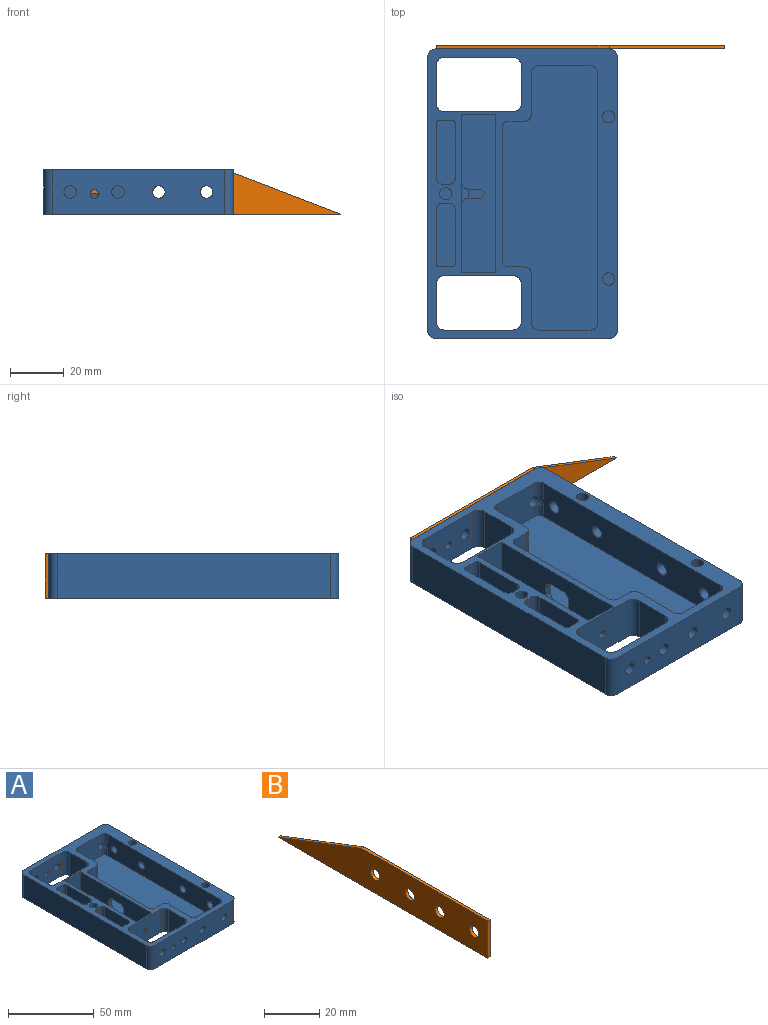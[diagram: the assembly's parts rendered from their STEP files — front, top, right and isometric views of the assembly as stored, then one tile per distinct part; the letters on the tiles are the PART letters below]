
ASSEMBLY  parts=2 mates=1
PART A: 110 faces, bbox 70.7x108x16.5 mm
  f0: plane 107.95x70.68mm, normal (0,0,1), area 2195.9mm2, adj f1,f2,f3,f7,f8,f9,f11,f12
  f1: plane 101.6x16.51mm, normal (1,0,0), area 1608mm2, adj f0,f14,f31,f32,f97,f98,f99,f100
  f2: plane 95.95x15.24mm, normal (-1,0,0), area 1357mm2, adj f0,f34,f85,f86,f87,f88,f89,f90
  f3: plane 49.23x15.24mm, normal (1,0,0), area 648.4mm2, adj f0,f34,f70,f71,f72,f73,f74,f75
  f4: plane 6.35x4.9mm, normal (0,1,0), area 31.1mm2, adj f6,f34,f102,f105
  f5: plane 6.35x4.9mm, normal (0,-1,0), area 31.1mm2, adj f6,f34,f101,f103
  f6: plane 6.52x3.24mm, normal (0,0,1), area 18.5mm2, adj f4,f5,f101,f102,f104
  f7: plane 64.33x16.51mm, normal (0,1,0), area 984.4mm2, adj f0,f11,f31,f32,f59,f66,f67,f68
  f8: plane 64.33x16.51mm, normal (0,-1,0), area 984.4mm2, adj f0,f13,f14,f32,f58,f62,f63,f64
  f9: plane 58.93x15.24mm, normal (1,0,0), area 824.1mm2, adj f0,f34,f60,f61,f103,f104,f105
  f10: cylinder r=1.63mm len=3.27mm, axis (0,-1,0), area 10.4mm2, adj f15,f60
  f11: cylinder r=3.17mm len=16.51mm, axis (0,0,-1), area 82.3mm2, adj f0,f7,f12,f32
  f12: plane 101.6x16.51mm, normal (-1,0,0), area 1677.4mm2, adj f0,f11,f13,f32
  f13: cylinder r=3.17mm len=16.51mm, axis (0,0,-1), area 82.3mm2, adj f0,f8,f12,f32
  f14: cylinder r=3.17mm len=16.51mm, axis (0,0,-1), area 82.3mm2, adj f0,f1,f8,f32
  f15: plane 25.4x16.51mm, normal (0,1,0), area 411mm2, adj f0,f10,f16,f29,f32
  f16: cylinder r=3.17mm len=16.51mm, axis (0,0,-1), area 82.3mm2, adj f0,f15,f17,f32
  f17: plane 16.51x13.97mm, normal (1,0,0), area 230.6mm2, adj f0,f16,f18,f32
  f18: cylinder r=3.17mm len=16.51mm, axis (0,0,-1), area 82.3mm2, adj f0,f17,f19,f32
  f19: plane 25.4x16.51mm, normal (0,-1,0), area 376.3mm2, adj f0,f18,f20,f32,f59,f68,f69
  f20: cylinder r=3.17mm len=16.51mm, axis (0,0,-1), area 82.3mm2, adj f0,f19,f21,f32
  f21: plane 16.51x13.97mm, normal (-1,0,0), area 230.6mm2, adj f0,f20,f29,f32
  f22: cylinder r=3.17mm len=16.51mm, axis (0,0,-1), area 82.3mm2, adj f0,f23,f30,f32
  f23: plane 25.4x16.51mm, normal (0,-1,0), area 411mm2, adj f0,f22,f24,f32,f57
  f24: cylinder r=3.17mm len=16.51mm, axis (0,0,-1), area 82.3mm2, adj f0,f23,f25,f32
  f25: plane 16.51x13.97mm, normal (-1,0,0), area 230.6mm2, adj f0,f24,f26,f32
  f26: cylinder r=3.17mm len=16.51mm, axis (0,0,-1), area 82.3mm2, adj f0,f25,f27,f32
  f27: plane 25.4x16.51mm, normal (0,1,0), area 376.3mm2, adj f0,f26,f28,f32,f58,f64,f65
  f28: cylinder r=3.17mm len=16.51mm, axis (0,0,-1), area 82.3mm2, adj f0,f27,f30,f32
  f29: cylinder r=3.17mm len=16.51mm, axis (0,0,-1), area 82.3mm2, adj f0,f15,f21,f32
  f30: plane 16.51x13.97mm, normal (1,0,0), area 230.6mm2, adj f0,f22,f28,f32
  f31: cylinder r=3.17mm len=16.51mm, axis (0,0,-1), area 82.3mm2, adj f0,f1,f7,f32
  f32: plane 107.95x70.68mm, normal (0,0,-1), area 6348.6mm2, adj f1,f7,f8,f11,f12,f13,f14,f15
  f33: plane 58.93x15.24mm, normal (-1,0,0), area 796.1mm2, adj f0,f34,f60,f61,f70,f71,f72,f73
  f34: plane 98.43x50.75mm, normal (0,0,1), area 3756.6mm2, adj f2,f3,f4,f5,f9,f33,f51,f52
  f35: cylinder r=1.27mm len=15.24mm, axis (0,0,1), area 30.4mm2, adj f0,f36,f40,f41
  f36: plane 15.24x4.56mm, normal (0,-1,0), area 69.5mm2, adj f0,f35,f37,f41
  f37: cylinder r=1.27mm len=15.24mm, axis (0,0,1), area 30.4mm2, adj f0,f36,f38,f41
  f38: plane 20.01x15.24mm, normal (1,0,0), area 304.9mm2, adj f0,f37,f41,f79
  f39: plane 15.24x2.02mm, normal (0,1,0), area 30.8mm2, adj f0,f41,f79,f80
  f40: plane 20.01x15.24mm, normal (-1,0,0), area 304.9mm2, adj f0,f35,f41,f80
  f41: plane 23.82x7.1mm, normal (0,0,1), area 165.6mm2, adj f35,f36,f37,f38,f39,f40,f79,f80
  f42: plane 15.24x2.02mm, normal (0,-1,0), area 30.8mm2, adj f0,f48,f77,f78
  f43: plane 20.01x15.24mm, normal (1,0,0), area 304.9mm2, adj f0,f44,f48,f78
  f44: cylinder r=1.27mm len=15.24mm, axis (0,0,1), area 30.4mm2, adj f0,f43,f45,f48
  f45: plane 15.24x4.56mm, normal (0,1,0), area 69.5mm2, adj f0,f44,f46,f48
  f46: cylinder r=1.27mm len=15.24mm, axis (0,0,1), area 30.4mm2, adj f0,f45,f47,f48
  f47: plane 20.01x15.24mm, normal (-1,0,0), area 304.9mm2, adj f0,f46,f48,f77
  f48: plane 23.82x7.1mm, normal (0,0,1), area 165.6mm2, adj f42,f43,f44,f45,f46,f47,f77,f78
  f49: cylinder r=2.29mm len=15.24mm, axis (0,0,1), area 218.9mm2, adj f0,f50
  f50: plane 4.57x4.57mm, normal (0,0,1), area 16.4mm2, adj f49
  f51: plane 15.24x5.87mm, normal (0,-1,0), area 89.5mm2, adj f0,f34,f81,f96
  f52: plane 15.24x5.87mm, normal (0,1,0), area 89.5mm2, adj f0,f34,f94,f95
  f53: plane 18.5x15.24mm, normal (1,0,0), area 280.8mm2, adj f0,f34,f91,f92,f93,f94
  f54: plane 19.66x15.24mm, normal (0,1,0), area 274.2mm2, adj f0,f34,f62,f63,f88,f90,f91,f93
  f55: plane 19.66x15.24mm, normal (0,-1,0), area 274.3mm2, adj f0,f34,f66,f67,f82,f84,f85,f87
  f56: plane 15.6x15.24mm, normal (1,0,0), area 236.9mm2, adj f0,f34,f81,f82,f83,f84
  f57: cylinder r=1.63mm len=3.27mm, axis (0,-1,0), area 10.4mm2, adj f23,f61
  f58: cylinder r=1.63mm len=3.27mm, axis (0,-1,0), area 32.6mm2, adj f8,f27
  f59: cylinder r=1.63mm len=3.27mm, axis (0,-1,0), area 32.6mm2, adj f7,f19
  f60: plane 15.24x12.7mm, normal (0,-1,0), area 185.2mm2, adj f0,f9,f10,f33,f34
  f61: plane 15.24x12.7mm, normal (0,1,0), area 185.2mm2, adj f0,f9,f33,f34,f57
  f62: cylinder r=2.35mm len=4.7mm, axis (0,-1,0), area 46.9mm2, adj f8,f54,f89
  f63: cylinder r=2.35mm len=4.7mm, axis (0,-1,0), area 46.9mm2, adj f8,f54,f92
  f64: cylinder r=2.35mm len=4.7mm, axis (0,-1,0), area 46.9mm2, adj f8,f27
  f65: cylinder r=2.35mm len=4.7mm, axis (0,-1,0), area 46.9mm2, adj f8,f27
  f66: cylinder r=2.35mm len=6.35mm, axis (0,1,0), area 93.7mm2, adj f7,f55,f83
  f67: cylinder r=2.35mm len=6.35mm, axis (0,1,0), area 93.7mm2, adj f7,f55,f86
  f68: cylinder r=2.35mm len=4.7mm, axis (0,1,0), area 46.9mm2, adj f7,f19
  f69: cylinder r=2.35mm len=4.7mm, axis (0,1,0), area 46.9mm2, adj f7,f19
  f70: plane 2.73x2.36mm, normal (0,1,0), area 6.4mm2, adj f3,f33,f71,f76
  f71: cylinder r=3.17mm len=3.18mm, axis (1,0,0), area 11.8mm2, adj f3,f33,f34,f70
  f72: cylinder r=3.17mm len=3.18mm, axis (1,0,0), area 11.8mm2, adj f3,f33,f34,f73
  f73: plane 2.73x2.36mm, normal (0,-1,0), area 6.4mm2, adj f3,f33,f72,f74
  f74: cylinder r=3.17mm len=3.18mm, axis (1,0,0), area 11.8mm2, adj f3,f33,f73,f75
  f75: plane 5.83x2.36mm, normal (0,0,-1), area 13.7mm2, adj f3,f33,f74,f76
  f76: cylinder r=3.17mm len=3.18mm, axis (1,0,0), area 11.8mm2, adj f3,f33,f70,f75
  f77: cylinder r=2.54mm len=15.24mm, axis (0,0,1), area 60.8mm2, adj f0,f42,f47,f48
  f78: cylinder r=2.54mm len=15.24mm, axis (0,0,-1), area 60.8mm2, adj f0,f42,f43,f48
  f79: cylinder r=2.54mm len=15.24mm, axis (0,0,1), area 60.8mm2, adj f0,f38,f39,f41
  f80: cylinder r=2.54mm len=15.24mm, axis (0,0,-1), area 60.8mm2, adj f0,f39,f40,f41
  f81: cylinder r=2.54mm len=15.24mm, axis (0,0,-1), area 60.8mm2, adj f0,f34,f51,f56
  f82: cylinder r=2.54mm len=6.72mm, axis (0,0,-1), area 26.8mm2, adj f0,f55,f56,f83
  f83: bspline ~3.69x2.73mm, area 10.9mm2, adj f56,f66,f82,f84
  f84: cylinder r=2.54mm len=5.49mm, axis (0,0,-1), area 21.9mm2, adj f34,f55,f56,f83
  f85: cylinder r=2.54mm len=5.88mm, axis (0,0,1), area 23.5mm2, adj f0,f2,f55,f86
  f86: bspline ~5.39x2.56mm, area 12.2mm2, adj f2,f67,f85,f87
  f87: cylinder r=2.54mm len=4.66mm, axis (0,0,1), area 18.6mm2, adj f2,f34,f55,f86
  f88: cylinder r=2.54mm len=5.91mm, axis (0,0,-1), area 23.6mm2, adj f0,f2,f54,f89
  f89: bspline ~5.28x2.57mm, area 11.7mm2, adj f2,f62,f88,f90
  f90: cylinder r=2.54mm len=4.64mm, axis (0,0,-1), area 18.5mm2, adj f2,f34,f54,f89
  f91: cylinder r=2.54mm len=6.62mm, axis (0,0,-1), area 26.4mm2, adj f0,f53,f54,f92
  f92: bspline ~3.26x2.54mm, area 11.5mm2, adj f53,f63,f91,f93
  f93: cylinder r=2.54mm len=5.35mm, axis (0,0,-1), area 21.4mm2, adj f34,f53,f54,f92
  f94: cylinder r=2.54mm len=15.24mm, axis (0,0,1), area 60.8mm2, adj f0,f34,f52,f53
  f95: cylinder r=2.54mm len=15.24mm, axis (0,0,-1), area 60.8mm2, adj f0,f3,f34,f52
  f96: cylinder r=2.54mm len=15.24mm, axis (0,0,-1), area 60.8mm2, adj f0,f3,f34,f51
  f97: cylinder r=2.35mm len=7.24mm, axis (1,0,0), area 106.8mm2, adj f1,f2
  f98: cylinder r=2.35mm len=7.24mm, axis (1,0,0), area 106.8mm2, adj f1,f2
  f99: cylinder r=2.35mm len=7.24mm, axis (1,0,0), area 106.8mm2, adj f1,f2
  f100: cylinder r=2.35mm len=7.24mm, axis (1,0,0), area 106.8mm2, adj f1,f2
  f101: plane 6.35x1.62mm, normal (0.71,-0.71,0), area 14.5mm2, adj f5,f6,f34,f102
  f102: plane 6.35x1.62mm, normal (0.71,0.71,0), area 14.5mm2, adj f4,f6,f34,f101
  f103: cylinder r=2.54mm len=8.89mm, axis (0,0,1), area 30.4mm2, adj f5,f9,f34,f104
  f104: cylinder r=2.54mm len=8.32mm, axis (0,-1,0), area 23mm2, adj f6,f9,f103,f105
  f105: cylinder r=2.54mm len=8.89mm, axis (0,0,-1), area 30.4mm2, adj f4,f9,f34,f104
  f106: cylinder r=2.29mm len=11.43mm, axis (0,0,1), area 164.2mm2, adj f0,f107
  f107: plane 4.57x4.57mm, normal (0,0,1), area 16.4mm2, adj f106
  f108: cylinder r=2.29mm len=11.43mm, axis (0,0,1), area 164.2mm2, adj f0,f109
  f109: plane 4.57x4.57mm, normal (0,0,1), area 16.4mm2, adj f108
PART B: 10 faces, bbox 1.3x107.3x16.5 mm
  f0: plane 64.33x1.27mm, normal (0,0,1), area 81.7mm2, adj f1,f7,f8,f9
  f1: plane 16.51x1.27mm, normal (0,-1,0), area 21mm2, adj f0,f2,f8,f9
  f2: plane 107.34x1.27mm, normal (0,0,-1), area 136.3mm2, adj f1,f7,f8,f9
  f3: cylinder r=2.35mm len=4.7mm, axis (-1,0,0), area 18.7mm2, adj f8,f9
  f4: cylinder r=2.35mm len=4.7mm, axis (-1,0,0), area 18.7mm2, adj f8,f9
  f5: cylinder r=2.35mm len=4.7mm, axis (-1,0,0), area 18.7mm2, adj f8,f9
  f6: cylinder r=2.35mm len=4.7mm, axis (-1,0,0), area 18.7mm2, adj f8,f9
  f7: plane 43x16.51mm, normal (0,0.36,0.93), area 58.5mm2, adj f0,f2,f8,f9
  f8: plane 107.34x16.51mm, normal (1,0,0), area 1347.8mm2, adj f0,f1,f2,f3,f4,f5,f6,f7
  f9: plane 107.34x16.51mm, normal (-1,0,0), area 1347.8mm2, adj f0,f1,f2,f3,f4,f5,f6,f7
PLACE A t=(-205.87,-155.22,68.39)mm
PLACE B rot(axis=(0,0,-1),90deg) t=(-172.93,-103.47,24.2)mm
MATE fastened B.f5 <-> A.f67  axis (0,-1,0) through (-206.84,-104.74,76.67)mm
